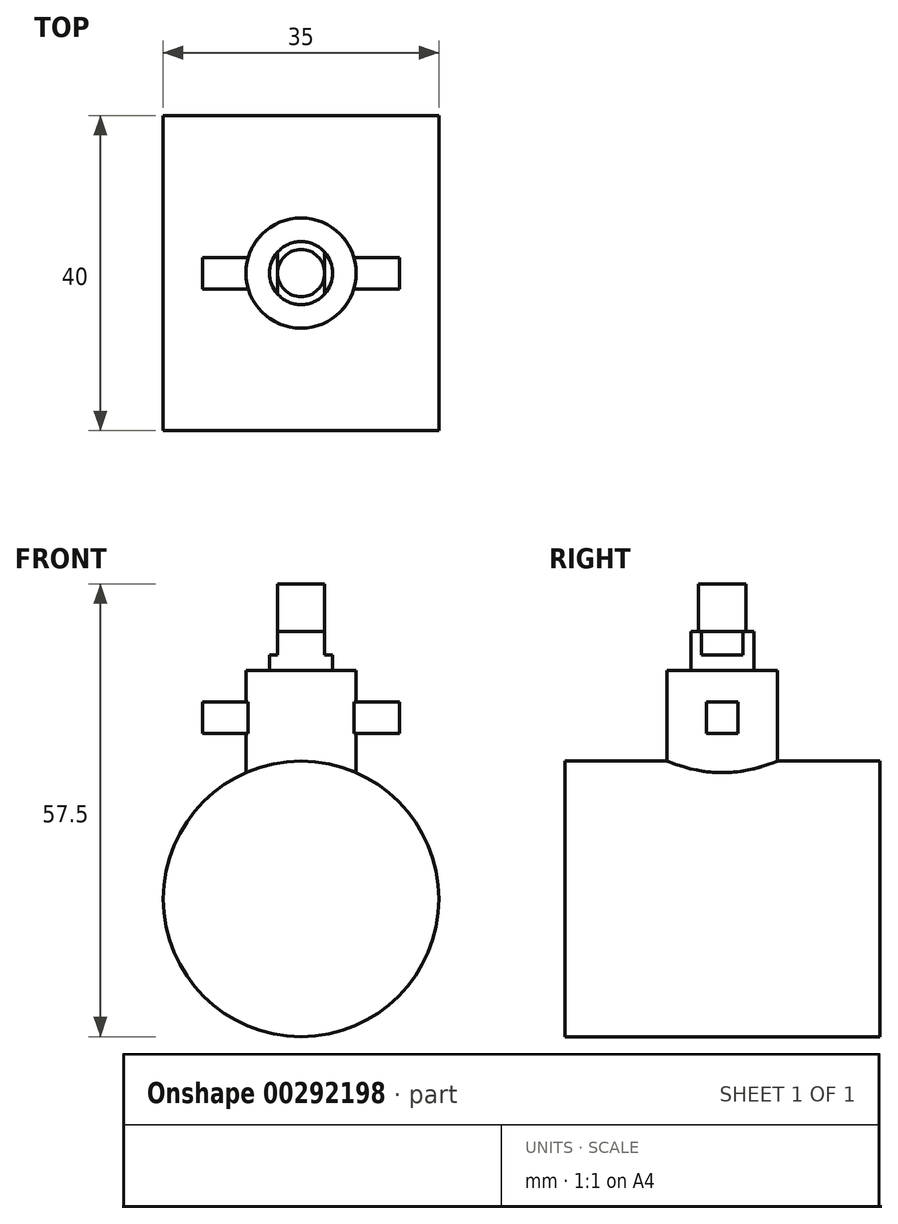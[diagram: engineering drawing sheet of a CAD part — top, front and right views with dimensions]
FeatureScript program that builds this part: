
annotation { "Feature Type Name" : "Feature", "Feature Type Description" : "" }
export const myFeature = defineFeature(function(context is Context, id is Id, definition is map)
    precondition{}
    {
        {
            var Q0;
            Q0=qCreatedBy(makeId("Front.planeOp"),FACE);
            var sketch = newSketch(context, id + "F0", { "sketchPlane" : qUnion([Q0])});
            skCircle(sketch, "E0", {"center": v(0, 0) * mm, "radius": 17.5 * mm});
            skSolve(sketch);
        }
        {
            var Q0;
            Q0=makeQuery(id+"F0.imprint","IMPRINT",FACE,{"disambiguationData":[TD([[makeQuery(id+"F0.imprint","IMPRINT",EDGE,{"derivedFrom":sQuery(id+"F0.wireOp",EDGE,"E0")}),1.0]])]});
            extrude(context, id + "F1", {"entities" : qUnion([Q0]), "endBound" : BoundingType.SYMMETRIC, "depth" : 40 * mm});
        }
        {
            var Q0;
            Q0=qCreatedBy(makeId("Top.planeOp"),FACE);
            var sketch = newSketch(context, id + "F2", { "sketchPlane" : qUnion([Q0])});
            skCircle(sketch, "E1", {"center": v(0, 0) * mm, "radius": 7 * mm});
            skSolve(sketch);
        }
        {
            var Q0;
            Q0 = qSketchRegion(id + "F2", true);
            extrude(context, id + "F3", {"entities" : qUnion([Q0]), "operationType" : NewBodyOperationType.ADD, "depth" : 29 * mm});
        }
        {
            var Q0;
            Q0=makeQuery(id+"F3.opExtrude","CAP_FACE",FACE,{"disambiguationData":[OSD([sQuery(id+"F2.wireOp",EDGE,"E1")])],"isStart":false});
            var sketch = newSketch(context, id + "F4", { "sketchPlane" : qUnion([Q0])});
            skCircle(sketch, "E2", {"center": v(0, 0) * mm, "radius": 4 * mm});
            skSolve(sketch);
        }
        {
            var Q0;
            Q0=makeQuery(id+"F4.imprint","IMPRINT",FACE,{"disambiguationData":[TD([[makeQuery(id+"F4.imprint","IMPRINT",EDGE,{"derivedFrom":sQuery(id+"F4.wireOp",EDGE,"E2")}),1.0]])]});
            extrude(context, id + "F5", {"entities" : qUnion([Q0]), "operationType" : NewBodyOperationType.ADD, "depth" : 2 * mm});
        }
        {
            var Q0;
            Q0=makeQuery(id+"F5.opExtrude","CAP_FACE",FACE,{"disambiguationData":[OSD([sQuery(id+"F4.wireOp",EDGE,"E2")])],"isStart":false});
            var sketch = newSketch(context, id + "F6", { "sketchPlane" : qUnion([Q0])});
            skPoint(sketch, "E3.middle", {"position": v(0, 0) * mm});
            skLineSegment(sketch, "E4", {"start": v(-3, -2.65) * mm, "end": v(-3, 2.65) * mm});
            skLineSegment(sketch, "E5", {"start": v(3, -2.65) * mm, "end": v(3, 2.65) * mm});
            skSolve(sketch);
        }
        {
            var Q0;
            {var subQ0=sQuery(id+"F6.wireOp",EDGE,"E4");Q0=makeQuery(id+"F6.imprint","IMPRINT",FACE,{"disambiguationData":[TD([[makeQuery(id+"F6.imprint","IMPRINT",EDGE,{"derivedFrom":subQ0}),-1.0]])]});}
            extrude(context, id + "F7", {"entities" : qUnion([Q0]), "operationType" : NewBodyOperationType.ADD, "depth" : 3 * mm});
        }
        {
            var Q0;
            Q0=makeQuery(id+"F7.opExtrude","CAP_FACE",FACE,{"disambiguationData":[OSD([sQuery(id+"F4.wireOp",EDGE,"E2"),sQuery(id+"F6.wireOp",EDGE,"E4"),sQuery(id+"F6.wireOp",EDGE,"E5")])],"isStart":false});
            var sketch = newSketch(context, id + "F8", { "sketchPlane" : qUnion([Q0])});
            skCircle(sketch, "E6", {"center": v(0, 0) * mm, "radius": 3 * mm});
            skSolve(sketch);
        }
        {
            var Q0;
            {var subQ0=sQuery(id+"F8.wireOp",EDGE,"E6");var subQ1=makeQuery(id+"F8.imprint","INTERSECT",VERTEX,{"derivedFrom":[makeQuery(id+"F7.opExtrude","CAP_EDGE",EDGE,{"disambiguationData":[OSD([sQuery(id+"F6.wireOp",EDGE,"E4")])],"isStart":false}),subQ0]});Q0=makeQuery(id+"F8.imprint","IMPRINT",FACE,{"disambiguationData":[TD([[makeQuery(id+"F8.imprint","IMPRINT",EDGE,{"disambiguationData":[TD([[subQ1,1.0]])],"derivedFrom":subQ0}),1.0]])]});}
            extrude(context, id + "F9", {"entities" : qUnion([Q0]), "operationType" : NewBodyOperationType.ADD, "depth" : 6 * mm});
        }
        {
            var Q0;
            Q0=qCreatedBy(makeId("Right.planeOp"),FACE);
            var sketch = newSketch(context, id + "F10", { "sketchPlane" : qUnion([Q0])});
            skLineSegment(sketch, "E7.bottom", {"start": v(2, 25) * mm, "end": v(-2, 25) * mm});
            skLineSegment(sketch, "E7.top", {"start": v(2, 21) * mm, "end": v(-2, 21) * mm});
            skLineSegment(sketch, "E7.left", {"start": v(2, 25) * mm, "end": v(2, 21) * mm});
            skLineSegment(sketch, "E7.right", {"start": v(-2, 25) * mm, "end": v(-2, 21) * mm});
            skPoint(sketch, "E7.middle", {"position": v(0, 23) * mm});
            skSolve(sketch);
        }
        {
            var Q0;
            Q0 = qSketchRegion(id + "F10", true);
            extrude(context, id + "F11", {"entities" : qUnion([Q0]), "operationType" : NewBodyOperationType.ADD, "endBound" : BoundingType.SYMMETRIC, "depth" : 25 * mm});
        }
    });
